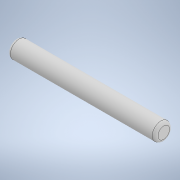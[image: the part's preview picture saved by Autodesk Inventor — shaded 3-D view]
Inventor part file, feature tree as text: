
AUTODESK INVENTOR PART (.ipt)
format: ipt  version: 2022 (Build 260153070, 153G)  size: 104,960 bytes
history: native  units: mm
features: fillet x2, extrude x1, sketch x1
ambient origin geometry x8: Origin, YZ Plane, XZ Plane, XY Plane, X Axis, Y Axis, Z Axis, Center Point
bodies: Solid1 (feature_tree)
feature tree (4):
  extrude  "Extrusion1"  Depth=50.8mm TaperAngle=0.0deg
  fillet  "Fillet1"  Radius=1.0mm
  fillet  "Fillet2"  Radius=1.0mm
  sketch  "Sketch1"  dims[d0=6.0mm d1=50.8mm d2=0.0mm d3=1.0mm d4=1.0mm]
